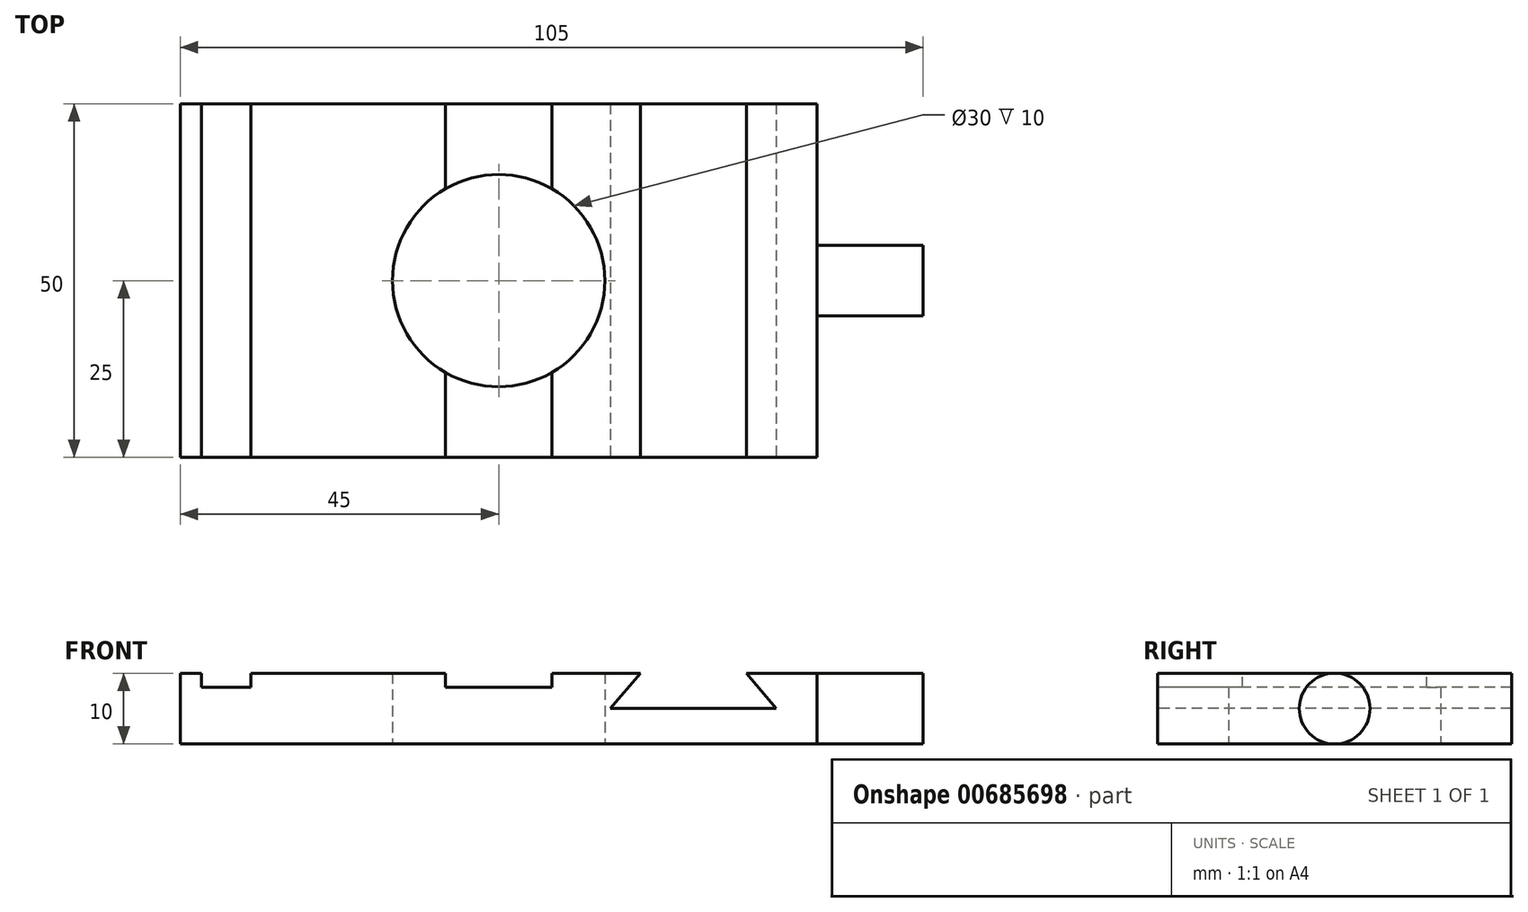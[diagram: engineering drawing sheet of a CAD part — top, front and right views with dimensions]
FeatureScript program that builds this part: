
annotation { "Feature Type Name" : "Feature", "Feature Type Description" : "" }
export const myFeature = defineFeature(function(context is Context, id is Id, definition is map)
    precondition{}
    {
        {
            var Q0;
            Q0=qCreatedBy(makeId("Top.planeOp"),FACE);
            var sketch = newSketch(context, id + "F0", { "sketchPlane" : qUnion([Q0])});
            skLineSegment(sketch, "E0.bottom", {"start": v(45, -25) * mm, "end": v(-45, -25) * mm});
            skLineSegment(sketch, "E0.top", {"start": v(45, 25) * mm, "end": v(-45, 25) * mm});
            skLineSegment(sketch, "E0.left", {"start": v(45, -25) * mm, "end": v(45, 25) * mm});
            skLineSegment(sketch, "E0.right", {"start": v(-45, -25) * mm, "end": v(-45, 25) * mm});
            skPoint(sketch, "E0.middle", {"position": v(0, 0) * mm});
            skCircle(sketch, "E1", {"center": v(0, 0) * mm, "radius": 15 * mm});
            skSolve(sketch);
        }
        {
            var Q0;
            Q0=makeQuery(id+"F0.imprint","IMPRINT",FACE,{"disambiguationData":[TD([[makeQuery(id+"F0.imprint","IMPRINT",EDGE,{"derivedFrom":sQuery(id+"F0.wireOp",EDGE,"E0.bottom")}),-1.0]])]});
            extrude(context, id + "F1", {"entities" : qUnion([Q0]), "depth" : 10 * mm, "offsetDistance" : 25 * mm});
        }
        {
            var Q0;
            Q0=makeQuery(id+"F1.opExtrude","CAP_FACE",FACE,{"disambiguationData":[OSD([sQuery(id+"F0.wireOp",EDGE,"E0.bottom"),sQuery(id+"F0.wireOp",EDGE,"E0.top"),sQuery(id+"F0.wireOp",EDGE,"E0.left"),sQuery(id+"F0.wireOp",EDGE,"E0.right"),sQuery(id+"F0.wireOp",EDGE,"E1")])],"isStart":false});
            var sketch = newSketch(context, id + "F2", { "sketchPlane" : qUnion([Q0])});
            skLineSegment(sketch, "E2.bottom", {"start": v(-42, 25) * mm, "end": v(-35, 25) * mm});
            skLineSegment(sketch, "E2.top", {"start": v(-42, -25) * mm, "end": v(-35, -25) * mm});
            skLineSegment(sketch, "E2.left", {"start": v(-42, 25) * mm, "end": v(-42, -25) * mm});
            skLineSegment(sketch, "E2.right", {"start": v(-35, 25) * mm, "end": v(-35, -25) * mm});
            skLineSegment(sketch, "E3", {"start": v(-7.5, 25) * mm, "end": v(-7.5, -25) * mm});
            skLineSegment(sketch, "E4", {"start": v(-7.5, -25) * mm, "end": v(7.5, -25) * mm});
            skLineSegment(sketch, "E5", {"start": v(7.5, -25) * mm, "end": v(7.5, 25) * mm});
            skLineSegment(sketch, "E6", {"start": v(7.5, 25) * mm, "end": v(-7.5, 25) * mm});
            skPoint(sketch, "E7", {"position": v(0, 0) * mm});
            skLineSegment(sketch, "E8", {"start": v(0, 25) * mm, "end": v(0, -25) * mm, "construction": true});
            skSolve(sketch);
        }
        {
            var Q0;
            Q0=makeQuery(id+"F2.imprint","IMPRINT",FACE,{"disambiguationData":[TD([[makeQuery(id+"F2.imprint","IMPRINT",EDGE,{"derivedFrom":sQuery(id+"F2.wireOp",EDGE,"E2.bottom")}),1.0]])]});
            var Q1;
            {var subQ0=sQuery(id+"F2.wireOp",EDGE,"E4");Q1=makeQuery(id+"F2.imprint","IMPRINT",FACE,{"disambiguationData":[TD([[makeQuery(id+"F2.imprint","IMPRINT",EDGE,{"derivedFrom":subQ0}),-1.0]])]});}
            var Q2;
            {var subQ0=sQuery(id+"F2.wireOp",EDGE,"E6");Q2=makeQuery(id+"F2.imprint","IMPRINT",FACE,{"disambiguationData":[TD([[makeQuery(id+"F2.imprint","IMPRINT",EDGE,{"derivedFrom":subQ0}),1.0]])]});}
            extrude(context, id + "F3", {"entities" : qUnion([Q0, Q1, Q2]), "operationType" : NewBodyOperationType.REMOVE, "oppositeDirection" : true, "depth" : 2 * mm, "offsetDistance" : 25 * mm});
        }
        {
            var Q0;
            Q0=makeQuery(id+"F1.opExtrude","SWEPT_FACE",FACE,{"disambiguationData":[OSD([sQuery(id+"F0.wireOp",EDGE,"E0.bottom")])]});
            var sketch = newSketch(context, id + "F4", { "sketchPlane" : qUnion([Q0])});
            skLineSegment(sketch, "E9", {"start": v(20, 10) * mm, "end": v(15.8, 5) * mm});
            skLineSegment(sketch, "E10", {"start": v(15.8, 5) * mm, "end": v(39.2, 5) * mm});
            skLineSegment(sketch, "E11", {"start": v(39.2, 5) * mm, "end": v(35, 10) * mm});
            skLineSegment(sketch, "E12", {"start": v(35, 10) * mm, "end": v(20, 10) * mm});
            skLineSegment(sketch, "E13", {"start": v(27.5, 5) * mm, "end": v(27.5, 10) * mm, "construction": true});
            skSolve(sketch);
        }
        {
            var Q0;
            Q0=makeQuery(id+"F4.imprint","IMPRINT",FACE,{"disambiguationData":[TD([[makeQuery(id+"F4.imprint","IMPRINT",EDGE,{"derivedFrom":sQuery(id+"F4.wireOp",EDGE,"E9")}),1.0]])]});
            extrude(context, id + "F5", {"entities" : qUnion([Q0]), "operationType" : NewBodyOperationType.REMOVE, "endBound" : BoundingType.THROUGH_ALL, "oppositeDirection" : true, "depth" : 50 * mm, "offsetDistance" : 25 * mm});
        }
        {
            var Q0;
            Q0=makeQuery(id+"F1.opExtrude","SWEPT_FACE",FACE,{"disambiguationData":[OSD([sQuery(id+"F0.wireOp",EDGE,"E0.left")])]});
            var sketch = newSketch(context, id + "F6", { "sketchPlane" : qUnion([Q0])});
            skCircle(sketch, "E14", {"center": v(0, 5) * mm, "radius": 5 * mm});
            skPoint(sketch, "E14.centerSnap0", {"position": v(-25, 5) * mm});
            skPoint(sketch, "E14.centerSnap1", {"position": v(0, 10) * mm});
            skSolve(sketch);
        }
        {
            var Q0;
            {var subQ0=sQuery(id+"F6.wireOp",EDGE,"E14");var subQ1=sQuery(id+"F0.wireOp",EDGE,"E0.left");var subQ2=makeQuery(id+"F6.imprint","INTERSECT",VERTEX,{"derivedFrom":[makeQuery(id+"F1.opExtrude","CAP_EDGE",EDGE,{"disambiguationData":[OSD([subQ1])],"isStart":true}),subQ0]});Q0=makeQuery(id+"F6.imprint","IMPRINT",FACE,{"disambiguationData":[TD([[makeQuery(id+"F6.imprint","IMPRINT",EDGE,{"disambiguationData":[TD([[subQ2,1.0]])],"derivedFrom":subQ0}),1.0]])]});}
            extrude(context, id + "F7", {"entities" : qUnion([Q0]), "operationType" : NewBodyOperationType.ADD, "depth" : 15 * mm, "offsetDistance" : 25 * mm});
        }
    });
